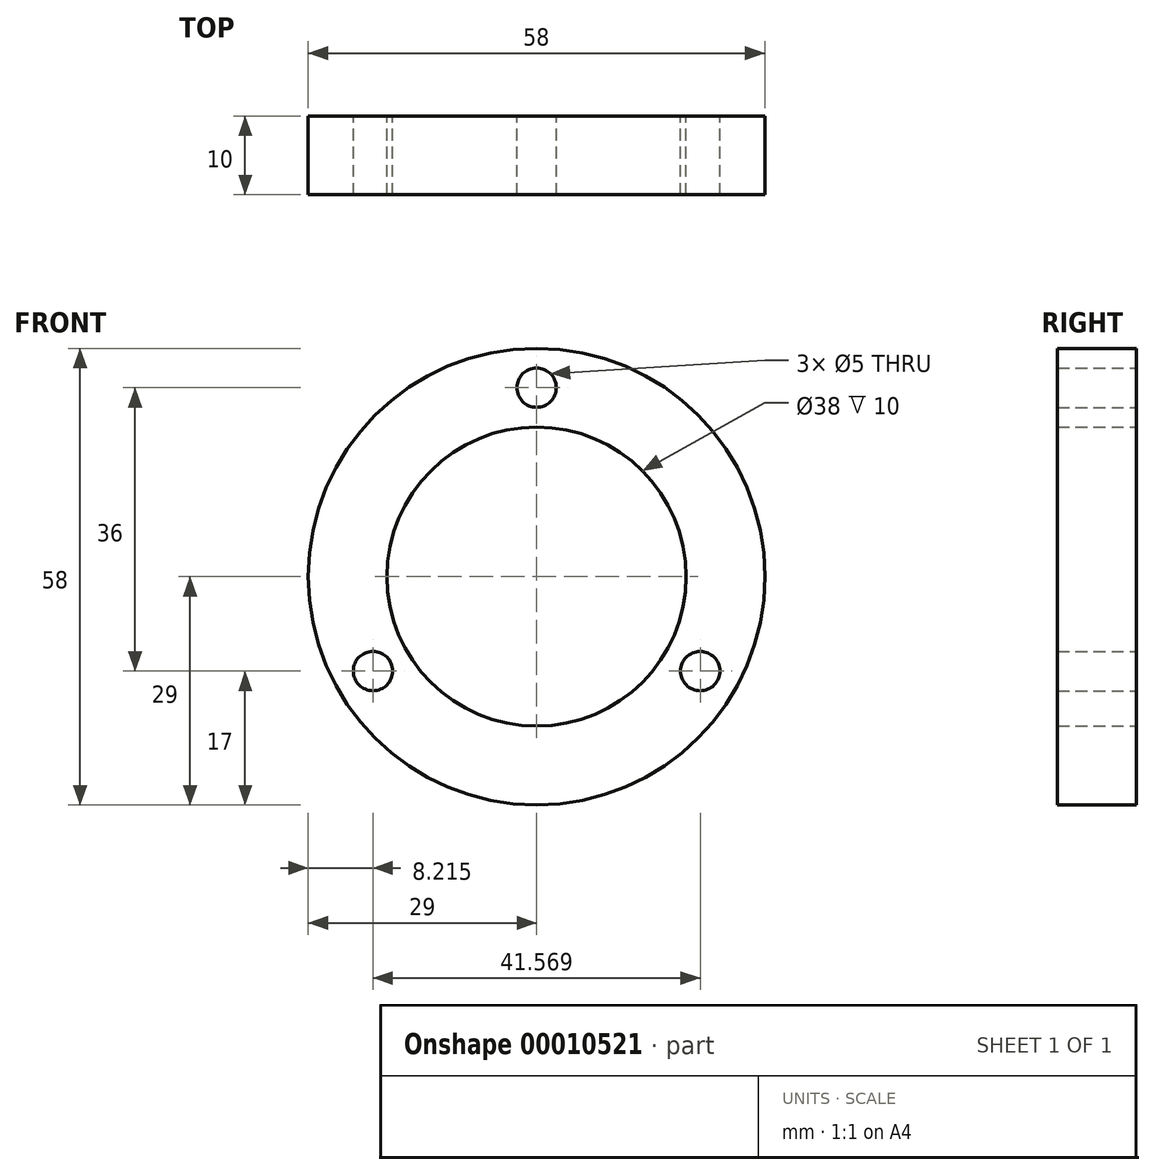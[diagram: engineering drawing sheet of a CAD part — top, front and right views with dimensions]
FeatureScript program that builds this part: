
annotation { "Feature Type Name" : "Feature", "Feature Type Description" : "" }
export const myFeature = defineFeature(function(context is Context, id is Id, definition is map)
    precondition{}
    {
        {
            var Q0;
            Q0=qCreatedBy(makeId("Front.planeOp"),FACE);
            var sketch = newSketch(context, id + "F0", { "sketchPlane" : qUnion([Q0])});
            skCircle(sketch, "E0", {"center": v(0, 0) * mm, "radius": 19 * mm});
            skCircle(sketch, "E1", {"center": v(0, 0) * mm, "radius": 29 * mm});
            skCircle(sketch, "E2", {"center": v(0, 24) * mm, "radius": 2.5 * mm});
            skLineSegment(sketch, "E3", {"start": v(0, 0) * mm, "end": v(0, 29) * mm});
            skCircle(sketch, "E4", {"center": v(-20.78, -12) * mm, "radius": 2.5 * mm});
            skLineSegment(sketch, "E5", {"start": v(0, 0) * mm, "end": v(-25.11, -14.5) * mm});
            skLineSegment(sketch, "E6", {"start": v(0, 0) * mm, "end": v(25.11, -14.5) * mm});
            skCircle(sketch, "E7", {"center": v(20.78, -12) * mm, "radius": 2.5 * mm});
            skLineSegment(sketch, "E8", {"start": v(0, 0) * mm, "end": v(29, 0) * mm});
            skLineSegment(sketch, "E9", {"start": v(0, 0) * mm, "end": v(-29, 0) * mm});
            skLineSegment(sketch, "E10", {"start": v(0, -180) * mm, "end": v(0, 0) * mm});
            skSolve(sketch);
        }
        {
            var Q0;
            Q0 = qSketchRegion(id + "F0", true);
            extrude(context, id + "F1", {"entities" : qUnion([Q0]), "depth" : 10 * mm});
        }
    });
